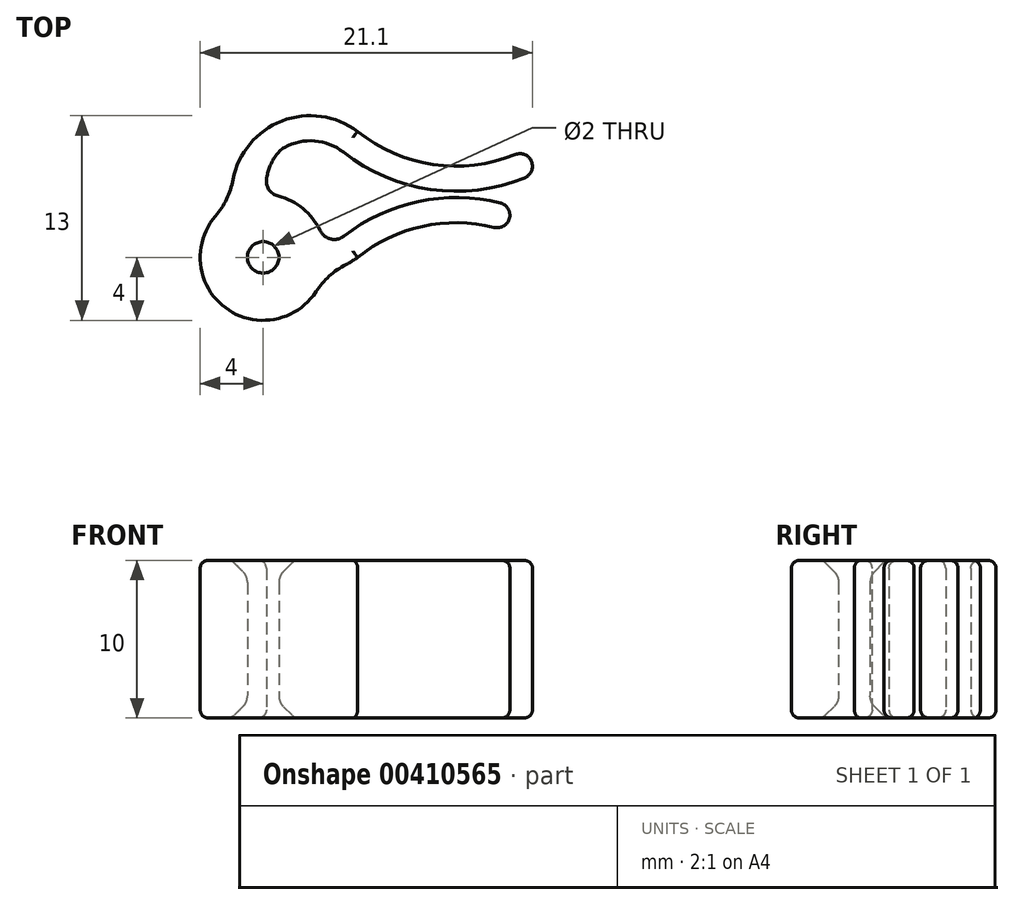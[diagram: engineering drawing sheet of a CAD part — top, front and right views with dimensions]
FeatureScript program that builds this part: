
annotation { "Feature Type Name" : "Feature", "Feature Type Description" : "" }
export const myFeature = defineFeature(function(context is Context, id is Id, definition is map)
    precondition{}
    {
        {
            var Q0;
            Q0=qCreatedBy(makeId("Top.planeOp"),FACE);
            var sketch = newSketch(context, id + "F0", { "sketchPlane" : qUnion([Q0])});
            skLineSegment(sketch, "E0", {"start": v(-5, 0) * mm, "end": v(13, 0) * mm, "construction": true});
            skArc(sketch, "E1", {"start": v(3, 4) * mm, "mid": v(7.8, 1.9) * mm, "end": v(13, 2.53) * mm});
            skLineSegment(sketch, "E2", {"start": v(-4.66, 1.8) * mm, "end": v(13, 1.8) * mm, "construction": true});
            skArc(sketch, "E3", {"start": v(2.1, 2.68) * mm, "mid": v(7.63, 0.32) * mm, "end": v(13.6, 1.05) * mm});
            skArc(sketch, "E4", {"start": v(2.1, 2.68) * mm, "mid": v(0.27, 3.4) * mm, "end": v(-1.64, 2.98) * mm});
            skArc(sketch, "E5.trimOffspring", {"start": v(3, 4) * mm, "mid": v(-2.24, 4.47) * mm, "end": v(-5, 0) * mm});
            skArc(sketch, "E6.MirrorCS", {"start": v(2.1, -2.68) * mm, "mid": v(6.84, -0.46) * mm, "end": v(12.06, -0.55) * mm});
            skArc(sketch, "E7.MirrorCS", {"start": v(2.1, -2.68) * mm, "mid": v(1.55, -3.03) * mm, "end": v(0.93, -3.27) * mm});
            skArc(sketch, "E8.MirrorCS", {"start": v(3, -4) * mm, "mid": v(2, -4.58) * mm, "end": v(0.9, -4.92) * mm});
            skArc(sketch, "E9.MirrorCS", {"start": v(3, -4) * mm, "mid": v(7.12, -2.03) * mm, "end": v(11.68, -2.1) * mm});
            skArc(sketch, "E10", {"start": v(0.93, -3.27) * mm, "mid": v(-0.4, -0.96) * mm, "end": v(-2.88, 0) * mm});
            skArc(sketch, "E11.trimOffspring", {"start": v(-3.4, -0.02) * mm, "mid": v(-3.4, -0.01) * mm, "end": v(-3.4, 0) * mm});
            skArc(sketch, "E12.trimOffspring", {"start": v(-4.97, -0.52) * mm, "mid": v(-5, -0.26) * mm, "end": v(-5, 0) * mm});
            skArc(sketch, "E13.trimOffspring", {"start": v(-4.97, -0.52) * mm, "mid": v(-5.4, -7.2) * mm, "end": v(0.9, -4.92) * mm});
            skCircle(sketch, "E14", {"center": v(-3, -4) * mm, "radius": 1 * mm});
            skLineSegment(sketch, "E15", {"start": v(12.06, -0.55) * mm, "end": v(11.68, -2.1) * mm, "construction": true});
            skLineSegment(sketch, "E16", {"start": v(13.6, 1.05) * mm, "end": v(13, 2.53) * mm, "construction": true});
            skLineSegment(sketch, "E17", {"start": v(9.26, -11.8) * mm, "end": v(9.26, 11.8) * mm, "construction": true});
            skArc(sketch, "E18", {"start": v(13.6, 1.05) * mm, "mid": v(14.04, 2.09) * mm, "end": v(13, 2.53) * mm});
            skArc(sketch, "E19", {"start": v(11.68, -2.1) * mm, "mid": v(12.64, -1.52) * mm, "end": v(12.06, -0.55) * mm});
            skEllipticalArc(sketch, "E20.trimOffspring", {});
            skPoint(sketch, "E21.trimOffspring.end.orphan", {"position": v(-3.4, 0) * mm});
            const initialGuessF0  = {"E20.trimOffspring": [-0.0011200990993529558, 0, 0, -1, 0.003120183561338733, 0.0017588601710472737, 3.442737857715125, 4.71297605673737]};
            skSetInitialGuess(sketch, initialGuessF0);
            skSolve(sketch);
        }
        {
            var Q0;
            Q0=makeQuery(id+"F0.imprint","IMPRINT",FACE,{"disambiguationData":[TD([[makeQuery(id+"F0.imprint","IMPRINT",EDGE,{"derivedFrom":sQuery(id+"F0.wireOp",EDGE,"E1")}),-1.0]])]});
            extrude(context, id + "F1", {"entities" : qUnion([Q0]), "depth" : 10 * mm});
        }
        {
            var Q0;
            Q0=makeQuery(id+"F1.opExtrude","CAP_EDGE",EDGE,{"disambiguationData":[OSD([sQuery(id+"F0.wireOp",EDGE,"E14")])],"isStart":false});
            var Q1;
            Q1=makeQuery(id+"F1.opExtrude","CAP_EDGE",EDGE,{"disambiguationData":[OSD([sQuery(id+"F0.wireOp",EDGE,"E14")])],"isStart":true});
            chamfer(context, id + "F2", {"entities" : qUnion([Q0, Q1]), "width" : 1 * mm, "tangentPropagation" : true});
        }
        {
            var Q0;
            Q0=makeQuery(id+"F1.opExtrude","SWEPT_EDGE",EDGE,{"disambiguationData":[OSD([sQuery(id+"F0.wireOp",EDGE,"E8.MirrorCS"),sQuery(id+"F0.wireOp",EDGE,"E13.trimOffspring")])]});
            var Q1;
            Q1=makeQuery(id+"F1.opExtrude","SWEPT_EDGE",EDGE,{"disambiguationData":[OSD([sQuery(id+"F0.wireOp",EDGE,"E12.trimOffspring"),sQuery(id+"F0.wireOp",EDGE,"E13.trimOffspring")])]});
            fillet(context, id + "F3", {"entities" : qUnion([Q0, Q1]), "radius" : 5 * mm, "tangentPropagation" : true, "allowEdgeOverflow" : false});
        }
        {
            var Q0;
            Q0=makeQuery(id+"F1.opExtrude","SWEPT_EDGE",EDGE,{"disambiguationData":[OSD([sQuery(id+"F0.wireOp",EDGE,"E7.MirrorCS"),sQuery(id+"F0.wireOp",EDGE,"E10")])]});
            var Q1;
            {var subQ0=sQuery(id+"F0.wireOp",EDGE,"E14");Q1=makeQuery(id+"F2.opChamfer","BLEND_EDGE",EDGE,{"blendedFrom":[makeQuery(id+"F1.opExtrude","CAP_EDGE",EDGE,{"disambiguationData":[OSD([subQ0])],"isStart":false}),makeQuery(id+"F1.opExtrude","SWEPT_FACE",FACE,{"disambiguationData":[OSD([subQ0])]})],"blendedInto":[makeQuery(id+"F1.opExtrude","SWEPT_FACE",FACE,{"disambiguationData":[OSD([subQ0])]})]});}
            var Q2;
            {var subQ0=sQuery(id+"F0.wireOp",EDGE,"E14");Q2=makeQuery(id+"F2.opChamfer","BLEND_EDGE",EDGE,{"blendedFrom":[makeQuery(id+"F1.opExtrude","CAP_EDGE",EDGE,{"disambiguationData":[OSD([subQ0])],"isStart":true}),makeQuery(id+"F1.opExtrude","SWEPT_FACE",FACE,{"disambiguationData":[OSD([subQ0])]})],"blendedInto":[makeQuery(id+"F1.opExtrude","SWEPT_FACE",FACE,{"disambiguationData":[OSD([subQ0])]})]});}
            var Q3;
            Q3=makeQuery(id+"F1.opExtrude","SWEPT_EDGE",EDGE,{"disambiguationData":[OSD([sQuery(id+"F0.wireOp",EDGE,"E10"),sQuery(id+"F0.wireOp",EDGE,"E20.trimOffspring")])]});
            fillet(context, id + "F4", {"entities" : qUnion([Q0, Q1, Q2, Q3]), "radius" : 1 * mm, "tangentPropagation" : true, "allowEdgeOverflow" : false});
        }
        {
            var Q0;
            Q0=makeQuery(id+"F1.opExtrude","CAP_EDGE",EDGE,{"disambiguationData":[OSD([sQuery(id+"F0.wireOp",EDGE,"8LgLwm9c-lEb3-tRGz-HdRu-wYf8BZgl2i80")])],"isStart":false});
            var Q1;
            Q1=makeQuery(id+"F1.opExtrude","CAP_EDGE",EDGE,{"disambiguationData":[OSD([sQuery(id+"F0.wireOp",EDGE,"E13.trimOffspring")])],"isStart":false});
            var Q2;
            {var subQ0=sQuery(id+"F0.wireOp",EDGE,"E14");Q2=makeQuery(id+"F2.opChamfer","BLEND_EDGE",EDGE,{"blendedFrom":[makeQuery(id+"F1.opExtrude","CAP_EDGE",EDGE,{"disambiguationData":[OSD([subQ0])],"isStart":false}),makeQuery(id+"F1.opExtrude","CAP_FACE",FACE,{"disambiguationData":[OSD([sQuery(id+"F0.wireOp",EDGE,"E1"),sQuery(id+"F0.wireOp",EDGE,"E3"),sQuery(id+"F0.wireOp",EDGE,"E4"),sQuery(id+"F0.wireOp",EDGE,"E5.trimOffspring"),sQuery(id+"F0.wireOp",EDGE,"E6.MirrorCS"),sQuery(id+"F0.wireOp",EDGE,"E7.MirrorCS"),sQuery(id+"F0.wireOp",EDGE,"E8.MirrorCS"),sQuery(id+"F0.wireOp",EDGE,"E9.MirrorCS"),sQuery(id+"F0.wireOp",EDGE,"E10"),sQuery(id+"F0.wireOp",EDGE,"E11.trimOffspring"),sQuery(id+"F0.wireOp",EDGE,"E12.trimOffspring"),sQuery(id+"F0.wireOp",EDGE,"E13.trimOffspring"),subQ0,sQuery(id+"F0.wireOp",EDGE,"8LgLwm9c-lEb3-tRGz-HdRu-wYf8BZgl2i80"),sQuery(id+"F0.wireOp",EDGE,"v6NCflSS-CFFQ-r9N9-mtmJ-q02JegzARBXb")])],"isStart":false})],"blendedInto":[makeQuery(id+"F1.opExtrude","CAP_FACE",FACE,{"disambiguationData":[OSD([sQuery(id+"F0.wireOp",EDGE,"E1"),sQuery(id+"F0.wireOp",EDGE,"E3"),sQuery(id+"F0.wireOp",EDGE,"E4"),sQuery(id+"F0.wireOp",EDGE,"E5.trimOffspring"),sQuery(id+"F0.wireOp",EDGE,"E6.MirrorCS"),sQuery(id+"F0.wireOp",EDGE,"E7.MirrorCS"),sQuery(id+"F0.wireOp",EDGE,"E8.MirrorCS"),sQuery(id+"F0.wireOp",EDGE,"E9.MirrorCS"),sQuery(id+"F0.wireOp",EDGE,"E10"),sQuery(id+"F0.wireOp",EDGE,"E11.trimOffspring"),sQuery(id+"F0.wireOp",EDGE,"E12.trimOffspring"),sQuery(id+"F0.wireOp",EDGE,"E13.trimOffspring"),subQ0,sQuery(id+"F0.wireOp",EDGE,"8LgLwm9c-lEb3-tRGz-HdRu-wYf8BZgl2i80"),sQuery(id+"F0.wireOp",EDGE,"v6NCflSS-CFFQ-r9N9-mtmJ-q02JegzARBXb")])],"isStart":false})]});}
            var Q3;
            Q3=makeQuery(id+"F1.opExtrude","CAP_EDGE",EDGE,{"disambiguationData":[OSD([sQuery(id+"F0.wireOp",EDGE,"v6NCflSS-CFFQ-r9N9-mtmJ-q02JegzARBXb")])],"isStart":true});
            var Q4;
            {var subQ0=sQuery(id+"F0.wireOp",EDGE,"E14");Q4=makeQuery(id+"F2.opChamfer","BLEND_EDGE",EDGE,{"blendedFrom":[makeQuery(id+"F1.opExtrude","CAP_EDGE",EDGE,{"disambiguationData":[OSD([subQ0])],"isStart":true}),makeQuery(id+"F1.opExtrude","CAP_FACE",FACE,{"disambiguationData":[OSD([sQuery(id+"F0.wireOp",EDGE,"E1"),sQuery(id+"F0.wireOp",EDGE,"E3"),sQuery(id+"F0.wireOp",EDGE,"E4"),sQuery(id+"F0.wireOp",EDGE,"E5.trimOffspring"),sQuery(id+"F0.wireOp",EDGE,"E6.MirrorCS"),sQuery(id+"F0.wireOp",EDGE,"E7.MirrorCS"),sQuery(id+"F0.wireOp",EDGE,"E8.MirrorCS"),sQuery(id+"F0.wireOp",EDGE,"E9.MirrorCS"),sQuery(id+"F0.wireOp",EDGE,"E10"),sQuery(id+"F0.wireOp",EDGE,"E11.trimOffspring"),sQuery(id+"F0.wireOp",EDGE,"E12.trimOffspring"),sQuery(id+"F0.wireOp",EDGE,"E13.trimOffspring"),subQ0,sQuery(id+"F0.wireOp",EDGE,"8LgLwm9c-lEb3-tRGz-HdRu-wYf8BZgl2i80"),sQuery(id+"F0.wireOp",EDGE,"v6NCflSS-CFFQ-r9N9-mtmJ-q02JegzARBXb")])],"isStart":true})],"blendedInto":[makeQuery(id+"F1.opExtrude","CAP_FACE",FACE,{"disambiguationData":[OSD([sQuery(id+"F0.wireOp",EDGE,"E1"),sQuery(id+"F0.wireOp",EDGE,"E3"),sQuery(id+"F0.wireOp",EDGE,"E4"),sQuery(id+"F0.wireOp",EDGE,"E5.trimOffspring"),sQuery(id+"F0.wireOp",EDGE,"E6.MirrorCS"),sQuery(id+"F0.wireOp",EDGE,"E7.MirrorCS"),sQuery(id+"F0.wireOp",EDGE,"E8.MirrorCS"),sQuery(id+"F0.wireOp",EDGE,"E9.MirrorCS"),sQuery(id+"F0.wireOp",EDGE,"E10"),sQuery(id+"F0.wireOp",EDGE,"E11.trimOffspring"),sQuery(id+"F0.wireOp",EDGE,"E12.trimOffspring"),sQuery(id+"F0.wireOp",EDGE,"E13.trimOffspring"),subQ0,sQuery(id+"F0.wireOp",EDGE,"8LgLwm9c-lEb3-tRGz-HdRu-wYf8BZgl2i80"),sQuery(id+"F0.wireOp",EDGE,"v6NCflSS-CFFQ-r9N9-mtmJ-q02JegzARBXb")])],"isStart":true})]});}
            var Q5;
            Q5=makeQuery(id+"F1.opExtrude","CAP_EDGE",EDGE,{"disambiguationData":[OSD([sQuery(id+"F0.wireOp",EDGE,"E13.trimOffspring")])],"isStart":true});
            var Q6;
            Q6=makeQuery(id+"F1.opExtrude","CAP_EDGE",EDGE,{"disambiguationData":[OSD([sQuery(id+"F0.wireOp",EDGE,"v6NCflSS-CFFQ-r9N9-mtmJ-q02JegzARBXb")])],"isStart":false});
            var Q7;
            Q7=makeQuery(id+"F1.opExtrude","CAP_EDGE",EDGE,{"disambiguationData":[OSD([sQuery(id+"F0.wireOp",EDGE,"E19")])],"isStart":false});
            var Q8;
            Q8=makeQuery(id+"F1.opExtrude","CAP_EDGE",EDGE,{"disambiguationData":[OSD([sQuery(id+"F0.wireOp",EDGE,"E19")])],"isStart":true});
            fillet(context, id + "F5", {"entities" : qUnion([Q0, Q1, Q2, Q3, Q4, Q5, Q6, Q7, Q8]), "radius" : .5 * mm, "tangentPropagation" : true, "allowEdgeOverflow" : false});
        }
    });
